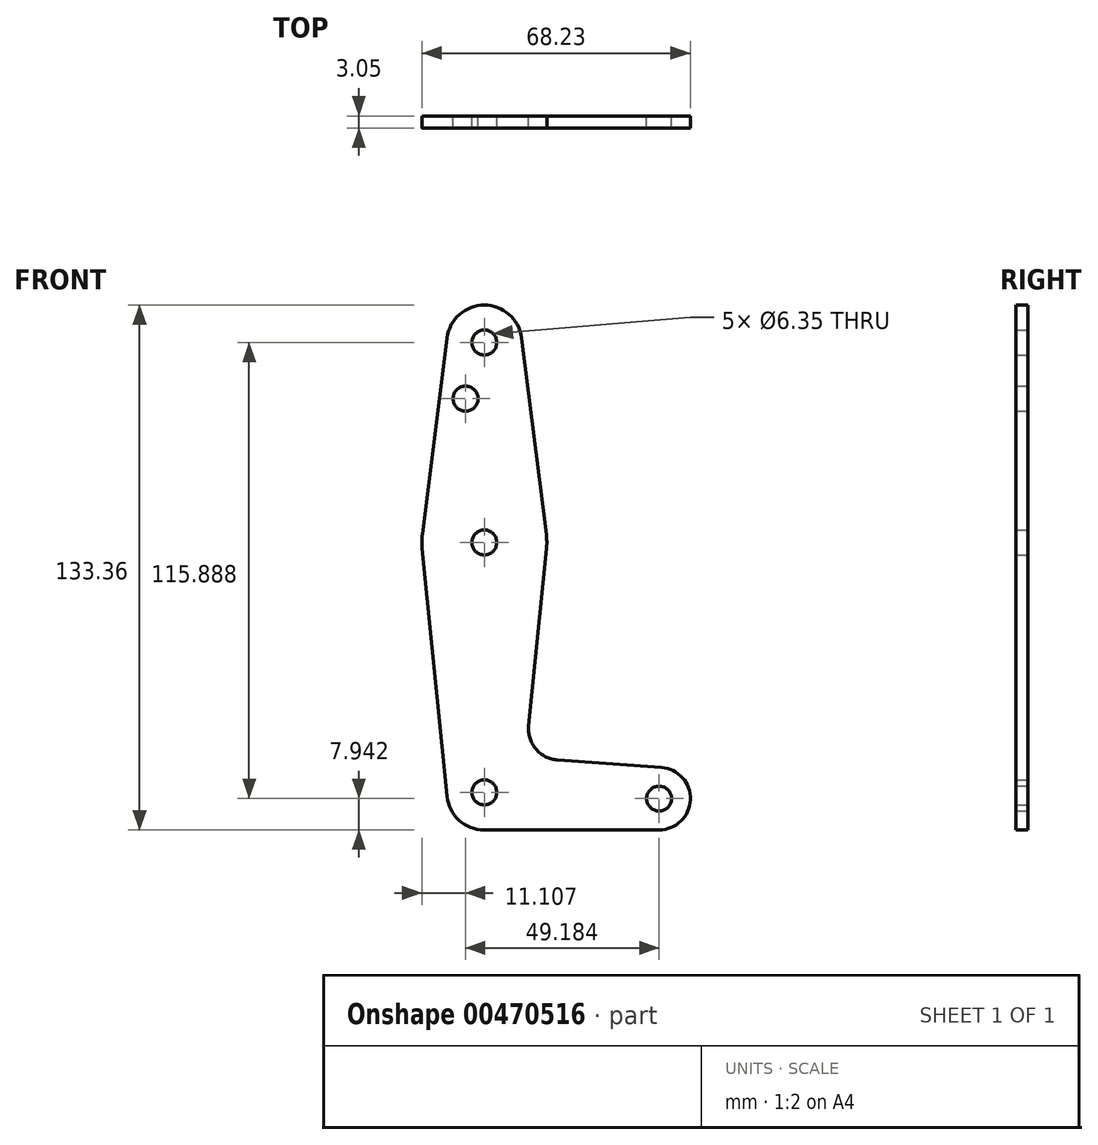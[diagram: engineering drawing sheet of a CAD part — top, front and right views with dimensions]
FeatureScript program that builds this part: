
annotation { "Feature Type Name" : "Feature", "Feature Type Description" : "" }
export const myFeature = defineFeature(function(context is Context, id is Id, definition is map)
    precondition{}
    {
        {
            var Q0;
            Q0=qCreatedBy(makeId("Front.planeOp"),FACE);
            var sketch = newSketch(context, id + "F0", { "sketchPlane" : qUnion([Q0])});
            skLineSegment(sketch, "E0", {"start": v(0, 0) * mm, "end": v(0, 114.3) * mm, "construction": true});
            skLineSegment(sketch, "E1", {"start": v(0, 0) * mm, "end": v(44.42, -1.59) * mm, "construction": true});
            skCircle(sketch, "E2", {"center": v(0, 114.3) * mm, "radius": 9.53 * mm});
            skCircle(sketch, "E3", {"center": v(0, 63.5) * mm, "radius": 15.88 * mm});
            skCircle(sketch, "E4", {"center": v(0, 0) * mm, "radius": 9.53 * mm});
            skCircle(sketch, "E5", {"center": v(44.42, -1.59) * mm, "radius": 7.94 * mm});
            skLineSegment(sketch, "E6", {"start": v(-9.45, 115.5) * mm, "end": v(-15.75, 65.48) * mm});
            skLineSegment(sketch, "E7", {"start": v(9.45, 115.5) * mm, "end": v(15.75, 65.48) * mm});
            skLineSegment(sketch, "E8", {"start": v(0, -9.53) * mm, "end": v(44.42, -9.52) * mm});
            skCircle(sketch, "E9", {"center": v(0, 63.5) * mm, "radius": 3.18 * mm});
            skCircle(sketch, "E10", {"center": v(0, 114.3) * mm, "radius": 3.18 * mm});
            skCircle(sketch, "E11", {"center": v(0, 0) * mm, "radius": 3.18 * mm});
            skCircle(sketch, "E12", {"center": v(44.42, -1.59) * mm, "radius": 3.18 * mm});
            skLineSegment(sketch, "E13", {"start": v(-15.8, 61.91) * mm, "end": v(-9.48, -0.95) * mm});
            skLineSegment(sketch, "E14", {"start": v(15.8, 61.91) * mm, "end": v(11.28, 16.94) * mm});
            skLineSegment(sketch, "E15", {"start": v(18.62, 8.22) * mm, "end": v(44.99, 6.33) * mm});
            skArc(sketch, "E16.filletArc", {"start": v(11.28, 16.94) * mm, "mid": v(13.1, 11.03) * mm, "end": v(18.62, 8.22) * mm});
            skCircle(sketch, "E17", {"center": v(-4.76, 100.03) * mm, "radius": 3.18 * mm});
            skSolve(sketch);
        }
        {
            var Q0;
            Q0 = qSketchRegion(id + "F0", true);
            extrude(context, id + "F1", {"entities" : qUnion([Q0]), "depth" : 3.05 * mm});
        }
    });
